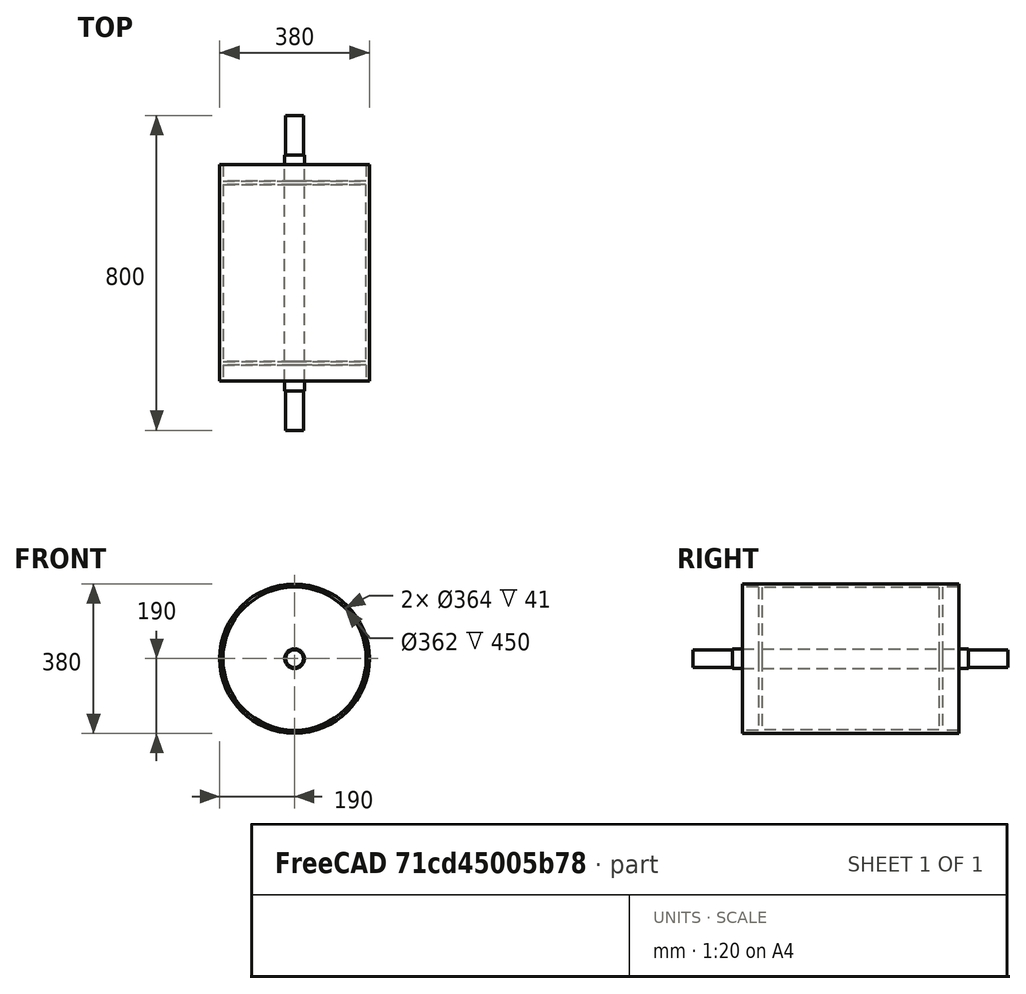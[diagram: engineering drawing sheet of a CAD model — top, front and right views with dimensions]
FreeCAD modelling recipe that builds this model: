
FCSTD DOCUMENT  (FreeCAD 1.0R39319 (Git))
Label: Take-Up_Assy
License: All rights reserved
LicenseURL: https://en.wikipedia.org/wiki/All_rights_reserved
objects: Sketcher::SketchObject×1, Spreadsheet::Sheet×1, Part::FeaturePython×1, App::Part×1
note: 3 computed .brp shape members not serialized (recipe doc carries the construction recipe); baked Part::Feature solids carry a one-line shape summary decoded from their .brp

FEATURE [Sketcher::SketchObject] Sketch
  ArcFitTolerance = 0
  FullyConstrained = true
  MakeInternals = false
  sketch-geometry (10):
    g0: LineSegment StartX=-600 StartY=-625 StartZ=0 EndX=-600 EndY=625 EndZ=0
    g1: LineSegment StartX=-600 StartY=625 StartZ=0 EndX=600 EndY=625 EndZ=0
    g2: LineSegment StartX=600 StartY=625 StartZ=0 EndX=600 EndY=-625 EndZ=0
    g3: LineSegment StartX=600 StartY=-625 StartZ=0 EndX=-600 EndY=-625 EndZ=0
    g4: GeomPoint [constr] X=0 Y=0 Z=0
    g5: LineSegment StartX=-525 StartY=-550 StartZ=0 EndX=-525 EndY=550 EndZ=0
    g6: LineSegment StartX=-525 StartY=550 StartZ=0 EndX=525 EndY=550 EndZ=0
    g7: LineSegment StartX=525 StartY=550 StartZ=0 EndX=525 EndY=-550 EndZ=0
    g8: LineSegment StartX=525 StartY=-550 StartZ=0 EndX=-525 EndY=-550 EndZ=0
    g9: GeomPoint [constr] X=0 Y=0 Z=0
  constraints (24):
    c: Coincident(g0,g1)
    c: Coincident(g1,g2)
    c: Coincident(g2,g3)
    c: Coincident(g3,g0)
    c: Horizontal(g1)
    c: Horizontal(g3)
    c: Vertical(g0)
    c: Vertical(g2)
    c: Symmetric(g1,g0,g4)
    c: Coincident(g4,g-1)
    c: Distance(g0) = 1250
    c: Distance(g4,g0) = 600
    c: Coincident(g5,g6)
    c: Coincident(g6,g7)
    c: Coincident(g7,g8)
    c: Coincident(g8,g5)
    c: Horizontal(g6)
    c: Horizontal(g8)
    c: Vertical(g5)
    c: Vertical(g7)
    c: Symmetric(g6,g5,g9)
    c: Coincident(g9,g4)
    c: Distance(g5,g0) = 75
    c: Distance(g5,g1) = 75
FEATURE [Spreadsheet::Sheet] Spreadsheet  label="Spreadsheet_takeup"
  cells = A1='beltWidth; B1='takeup d0; C1='d1=d0+10; D1='pulley D0; E1='puller L0; F1='puller C0; G1='puller B0; H1='takeup Y; A2(W0)=500; B2(d0)=20; C2(d1)==d0 + 10; D2(D0)=300; E2(L0)=550; F2(C0)=768; G2(B0)=50; H2(Y)=360; A3=400; B3=20; C3==d0 + 10; D3=300; E3=450; F3=568; G3=50; H3=310; A4=450; B4=20; C4==d0 + 10; D4=300; E4=500; F4=618; G4=50; H4=335; A5=500; B5=20; C5==d0 + 10; D5=300; E5=550; F5=668; G5=50; H5=360; A6=600; B6=20; C6==d0 + 10; D6=300; E6=650; F6=768; G6=50; H6=410; A7=700; B7=20; C7==d0 + 10; D7=300; E7=750; F7=868; G7=50; H7=460; A8=750; B8=20; C8==d0 + 10; D8=300; E8=800; F8=918; G8=50; H8=485; A9=800; B9=20; C9==d0 + 10; D9=300; E9=850; F9=968; G9=50; H9=510; A10=900; B10=20; C10==d0 + 10; D10=300; E10=950; F10=1068; G10=50; H10=560; A11=1000; B11=20; C11==d0 + 10; D11=300; E11=1050; F11=1168; G11=50; H11=610
FEATURE [Part::FeaturePython] Take_upPulley001  # WARN: FeaturePython — macro-defined, semantics opaque (R4)
  BeltWidth = 2
  D = 380
  E = 0
  L = 550
  Placement = pos=(0,0,0) rot=(0,0,1;1.5708rad)
  d1 = 50
  d2 = 45
  d3 = 0
FEATURE [App::Part] Part  label="takeUpAssy"
  Group = -> [Sketch,Spreadsheet,Take_upPulley001]
  JPN = テークアップアセンブリ
  Origin = -> Origin002
  count = 1
  mass = 77.1098
